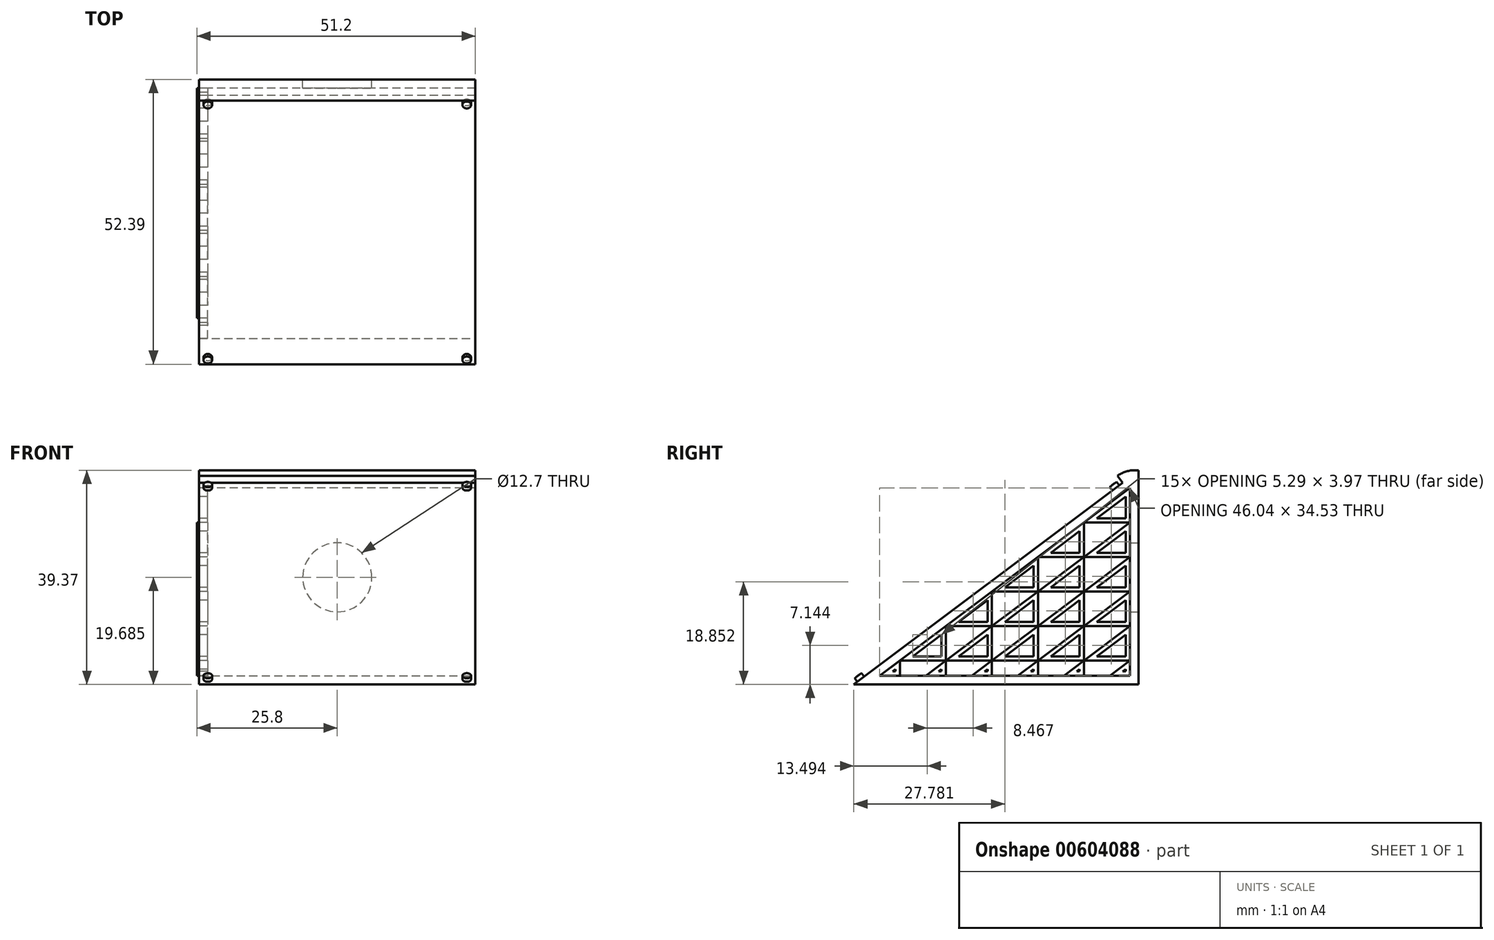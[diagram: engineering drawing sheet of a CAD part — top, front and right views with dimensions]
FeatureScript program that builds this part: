
annotation { "Feature Type Name" : "Feature", "Feature Type Description" : "" }
export const myFeature = defineFeature(function(context is Context, id is Id, definition is map)
    precondition{}
    {
        {
            var Q0;
            Q0=qCreatedBy(makeId("Right.planeOp"),FACE);
            var sketch = newSketch(context, id + "F0", { "sketchPlane" : qUnion([Q0])});
            skLineSegment(sketch, "E0.bottom", {"start": v(0, 0) * mm, "end": v(1.59, 0) * mm});
            skLineSegment(sketch, "E0.top", {"start": v(0, 38.1) * mm, "end": v(1.59, 38.1) * mm});
            skLineSegment(sketch, "E0.left", {"start": v(0, 0) * mm, "end": v(0, 36.12) * mm});
            skLineSegment(sketch, "E0.right", {"start": v(1.59, 0) * mm, "end": v(1.59, 38.1) * mm});
            skLineSegment(sketch, "E1", {"start": v(0, 38.1) * mm, "end": v(-50.8, 0) * mm});
            skLineSegment(sketch, "E2", {"start": v(-50.8, 0) * mm, "end": v(-48.15, 0) * mm});
            skLineSegment(sketch, "E3", {"start": v(-48.15, 0) * mm, "end": v(0, 36.12) * mm});
            skSolve(sketch);
        }
        {
            var Q0;
            Q0 = qSketchRegion(id + "F0", true);
            extrude(context, id + "F1", {"entities" : qUnion([Q0]), "depth" : 50.8 * mm, "offsetDistance" : 25.4 * mm});
        }
        {
            var Q0;
            Q0=makeQuery(id+"F1.opExtrude","SWEPT_FACE",FACE,{"disambiguationData":[OSD([sQuery(id+"F0.wireOp",EDGE,"E1")])]});
            var sketch = newSketch(context, id + "F2", { "sketchPlane" : qUnion([Q0])});
            skLineSegment(sketch, "E4.bottom", {"start": v(0, 22.86) * mm, "end": v(50.8, 22.86) * mm});
            skLineSegment(sketch, "E4.top", {"start": v(0, -40.64) * mm, "end": v(50.8, -40.64) * mm});
            skLineSegment(sketch, "E4.left", {"start": v(0, 22.86) * mm, "end": v(0, -40.64) * mm});
            skLineSegment(sketch, "E4.right", {"start": v(50.8, 22.86) * mm, "end": v(50.8, -40.64) * mm});
            skLineSegment(sketch, "E5.bottom", {"start": v(3.18, 19.69) * mm, "end": v(47.63, 19.69) * mm});
            skLineSegment(sketch, "E5.top", {"start": v(3.18, -37.47) * mm, "end": v(47.63, -37.47) * mm});
            skLineSegment(sketch, "E5.left", {"start": v(3.18, 19.69) * mm, "end": v(3.18, -37.47) * mm});
            skLineSegment(sketch, "E5.right", {"start": v(47.63, 19.69) * mm, "end": v(47.63, -37.47) * mm});
            skSolve(sketch);
        }
        {
            var Q0;
            Q0 = qSketchRegion(id + "F2", true);
            extrude(context, id + "F3", {"entities" : qUnion([Q0]), "operationType" : NewBodyOperationType.ADD, "depth" : 1.59 * mm, "offsetDistance" : 25.4 * mm});
        }
        {
            var Q0;
            Q0=makeQuery(id+"F3.boolean.opBoolean","MERGE",FACE,{"derivedFrom":[makeQuery(id+"F1.opExtrude","CAP_FACE",FACE,{"disambiguationData":[OSD([sQuery(id+"F0.wireOp",EDGE,"E0.bottom"),sQuery(id+"F0.wireOp",EDGE,"E0.top"),sQuery(id+"F0.wireOp",EDGE,"E0.left"),sQuery(id+"F0.wireOp",EDGE,"E0.right"),sQuery(id+"F0.wireOp",EDGE,"E1"),sQuery(id+"F0.wireOp",EDGE,"E2"),sQuery(id+"F0.wireOp",EDGE,"E3")])],"isStart":false}),makeQuery(id+"F3.opExtrude","SWEPT_FACE",FACE,{"disambiguationData":[OSD([sQuery(id+"F2.wireOp",EDGE,"E4.right")])]})]});
            var sketch = newSketch(context, id + "F4", { "sketchPlane" : qUnion([Q0])});
            skLineSegment(sketch, "E6", {"start": v(1.59, 38.1) * mm, "end": v(1.59, 39.37) * mm});
            skLineSegment(sketch, "E7", {"start": v(1.59, 39.37) * mm, "end": v(-0.95, 39.37) * mm});
            skLineSegment(sketch, "E8", {"start": v(-0.95, 39.37) * mm, "end": v(0, 38.1) * mm});
            skLineSegment(sketch, "E9", {"start": v(0, 38.1) * mm, "end": v(1.59, 38.1) * mm});
            skSolve(sketch);
        }
        {
            var Q0;
            Q0 = qSketchRegion(id + "F4", true);
            extrude(context, id + "F5", {"entities" : qUnion([Q0]), "operationType" : NewBodyOperationType.ADD, "oppositeDirection" : true, "depth" : 50.8 * mm, "offsetDistance" : 25.4 * mm});
        }
        {
            var Q0;
            Q0=makeQuery(id+"F5.boolean.opBoolean","MERGE",EDGE,{"derivedFrom":[makeQuery(id+"F3.opExtrude","CAP_EDGE",EDGE,{"disambiguationData":[OSD([sQuery(id+"F2.wireOp",EDGE,"E4.bottom")])],"isStart":false}),makeQuery(id+"F5.opExtrude","SWEPT_EDGE",EDGE,{"disambiguationData":[OSD([sQuery(id+"F2.wireOp",EDGE,"E4.right"),sQuery(id+"F4.wireOp",EDGE,"E7"),sQuery(id+"F4.wireOp",EDGE,"E8")])]})]});
            fillet(context, id + "F6", {"entities" : qUnion([Q0]), "radius" : 5.08 * mm, "tangentPropagation" : true, "allowEdgeOverflow" : false});
        }
        {
            var Q0;
            Q0=makeQuery(id+"F5.boolean.opBoolean","MERGE",FACE,{"derivedFrom":[makeQuery(id+"F1.opExtrude","SWEPT_FACE",FACE,{"disambiguationData":[OSD([sQuery(id+"F0.wireOp",EDGE,"E0.right")])]}),makeQuery(id+"F5.opExtrude","SWEPT_FACE",FACE,{"disambiguationData":[OSD([sQuery(id+"F4.wireOp",EDGE,"E6")])]})]});
            var sketch = newSketch(context, id + "F7", { "sketchPlane" : qUnion([Q0])});
            skCircle(sketch, "E10", {"center": v(-25.4, 19.69) * mm, "radius": 6.35 * mm});
            skPoint(sketch, "E10.centerSnap0", {"position": v(0, 19.69) * mm});
            skPoint(sketch, "E10.centerSnap1", {"position": v(-25.4, 39.37) * mm});
            skSolve(sketch);
        }
        {
            var Q0;
            Q0 = qSketchRegion(id + "F7", true);
            extrude(context, id + "F8", {"entities" : qUnion([Q0]), "operationType" : NewBodyOperationType.REMOVE, "oppositeDirection" : true, "depth" : 1.59 * mm, "offsetDistance" : 25.4 * mm});
        }
        {
            var Q0;
            Q0=makeQuery(id+"F3.opExtrude","CAP_FACE",FACE,{"disambiguationData":[OSD([sQuery(id+"F2.wireOp",EDGE,"E4.bottom"),sQuery(id+"F2.wireOp",EDGE,"E4.top"),sQuery(id+"F2.wireOp",EDGE,"E4.left"),sQuery(id+"F2.wireOp",EDGE,"E4.right"),sQuery(id+"F2.wireOp",EDGE,"E5.bottom"),sQuery(id+"F2.wireOp",EDGE,"E5.top"),sQuery(id+"F2.wireOp",EDGE,"E5.left"),sQuery(id+"F2.wireOp",EDGE,"E5.right")])],"isStart":false});
            var sketch = newSketch(context, id + "F9", { "sketchPlane" : qUnion([Q0])});
            skLineSegment(sketch, "E11.bottom", {"start": v(0, 21.17) * mm, "end": v(50.8, 21.17) * mm});
            skLineSegment(sketch, "E11.top", {"start": v(0, -40.64) * mm, "end": v(50.8, -40.64) * mm});
            skLineSegment(sketch, "E11.left", {"start": v(0, 21.17) * mm, "end": v(0, -40.64) * mm});
            skLineSegment(sketch, "E11.right", {"start": v(50.8, 21.17) * mm, "end": v(50.8, -40.64) * mm});
            skLineSegment(sketch, "E12.bottom", {"start": v(3.18, 19.69) * mm, "end": v(47.63, 19.69) * mm});
            skLineSegment(sketch, "E12.top", {"start": v(3.18, -37.47) * mm, "end": v(47.63, -37.47) * mm});
            skLineSegment(sketch, "E12.left", {"start": v(3.18, 19.69) * mm, "end": v(3.18, -37.47) * mm});
            skLineSegment(sketch, "E12.right", {"start": v(47.63, 19.69) * mm, "end": v(47.63, -37.47) * mm});
            skSolve(sketch);
        }
        {
            var Q0;
            Q0 = qSketchRegion(id + "F9", true);
            extrude(context, id + "F10", {"entities" : qUnion([Q0]), "operationType" : NewBodyOperationType.REMOVE, "oppositeDirection" : true, "depth" : 1.59 * mm, "offsetDistance" : 25.4 * mm});
        }
        {
            var Q0;
            Q0=makeQuery(id+"F10.boolean.opBoolean","MERGE",FACE,{"derivedFrom":[makeQuery(id+"F1.opExtrude","SWEPT_FACE",FACE,{"disambiguationData":[OSD([sQuery(id+"F0.wireOp",EDGE,"E1")])]}),makeQuery(id+"F10.opExtrude","CAP_FACE",FACE,{"disambiguationData":[OSD([sQuery(id+"F9.wireOp",EDGE,"E11.bottom"),sQuery(id+"F9.wireOp",EDGE,"E11.top"),sQuery(id+"F9.wireOp",EDGE,"E11.left"),sQuery(id+"F9.wireOp",EDGE,"E11.right"),sQuery(id+"F9.wireOp",EDGE,"E12.bottom"),sQuery(id+"F9.wireOp",EDGE,"E12.top"),sQuery(id+"F9.wireOp",EDGE,"E12.left"),sQuery(id+"F9.wireOp",EDGE,"E12.right")])],"isStart":false})]});
            var sketch = newSketch(context, id + "F11", { "sketchPlane" : qUnion([Q0])});
            skCircle(sketch, "E13", {"center": v(1.59, 19.58) * mm, "radius": 0.8 * mm});
            skCircle(sketch, "E14", {"center": v(1.59, -39.05) * mm, "radius": 0.8 * mm});
            skCircle(sketch, "E15.MirrorC", {"center": v(49.21, -39.05) * mm, "radius": 0.8 * mm});
            skCircle(sketch, "E16.MirrorC", {"center": v(49.21, 19.58) * mm, "radius": 0.8 * mm});
            skSolve(sketch);
        }
        {
            var Q0;
            Q0 = qSketchRegion(id + "F11", true);
            extrude(context, id + "F12", {"entities" : qUnion([Q0]), "operationType" : NewBodyOperationType.ADD, "depth" : 0.8 * mm, "offsetDistance" : 25.4 * mm});
        }
        {
            var Q0;
            Q0=makeQuery(id+"F5.boolean.opBoolean","MERGE",FACE,{"derivedFrom":[makeQuery(id+"F3.boolean.opBoolean","MERGE",FACE,{"derivedFrom":[makeQuery(id+"F1.opExtrude","CAP_FACE",FACE,{"disambiguationData":[OSD([sQuery(id+"F0.wireOp",EDGE,"E0.bottom"),sQuery(id+"F0.wireOp",EDGE,"E0.top"),sQuery(id+"F0.wireOp",EDGE,"E0.left"),sQuery(id+"F0.wireOp",EDGE,"E0.right"),sQuery(id+"F0.wireOp",EDGE,"E1"),sQuery(id+"F0.wireOp",EDGE,"E2"),sQuery(id+"F0.wireOp",EDGE,"E3")])],"isStart":false}),makeQuery(id+"F3.opExtrude","SWEPT_FACE",FACE,{"disambiguationData":[OSD([sQuery(id+"F2.wireOp",EDGE,"E4.right")])]})]}),makeQuery(id+"F5.opExtrude","CAP_FACE",FACE,{"disambiguationData":[OSD([sQuery(id+"F4.wireOp",EDGE,"E6"),sQuery(id+"F4.wireOp",EDGE,"E7"),sQuery(id+"F4.wireOp",EDGE,"E8"),sQuery(id+"F4.wireOp",EDGE,"E9")])],"isStart":true})]});
            var sketch = newSketch(context, id + "F13", { "sketchPlane" : qUnion([Q0])});
            skLineSegment(sketch, "E17", {"start": v(-48.15, 0) * mm, "end": v(0, 0) * mm});
            skLineSegment(sketch, "E18", {"start": v(0, 0) * mm, "end": v(0, 1.59) * mm});
            skLineSegment(sketch, "E19", {"start": v(0, 1.59) * mm, "end": v(-46.04, 1.59) * mm});
            skLineSegment(sketch, "E20", {"start": v(-48.15, 0) * mm, "end": v(-46.04, 1.59) * mm});
            skLineSegment(sketch, "E21", {"start": v(0, 1.59) * mm, "end": v(0, 0) * mm});
            skSolve(sketch);
        }
        {
            var Q0;
            Q0 = qSketchRegion(id + "F13", true);
            extrude(context, id + "F14", {"entities" : qUnion([Q0]), "operationType" : NewBodyOperationType.ADD, "oppositeDirection" : true, "depth" : 50.8 * mm, "offsetDistance" : 25.4 * mm});
        }
        {
            var Q0;
            Q0=makeQuery(id+"F14.boolean.opBoolean","MERGE",FACE,{"derivedFrom":[makeQuery(id+"F5.boolean.opBoolean","MERGE",FACE,{"derivedFrom":[makeQuery(id+"F3.boolean.opBoolean","MERGE",FACE,{"derivedFrom":[makeQuery(id+"F1.opExtrude","CAP_FACE",FACE,{"disambiguationData":[OSD([sQuery(id+"F0.wireOp",EDGE,"E0.bottom"),sQuery(id+"F0.wireOp",EDGE,"E0.top"),sQuery(id+"F0.wireOp",EDGE,"E0.left"),sQuery(id+"F0.wireOp",EDGE,"E0.right"),sQuery(id+"F0.wireOp",EDGE,"E1"),sQuery(id+"F0.wireOp",EDGE,"E2"),sQuery(id+"F0.wireOp",EDGE,"E3")])],"isStart":true}),makeQuery(id+"F3.opExtrude","SWEPT_FACE",FACE,{"disambiguationData":[OSD([sQuery(id+"F2.wireOp",EDGE,"E4.left")])]})]}),makeQuery(id+"F5.opExtrude","CAP_FACE",FACE,{"disambiguationData":[OSD([sQuery(id+"F4.wireOp",EDGE,"E6"),sQuery(id+"F4.wireOp",EDGE,"E7"),sQuery(id+"F4.wireOp",EDGE,"E8"),sQuery(id+"F4.wireOp",EDGE,"E9")])],"isStart":false})]}),makeQuery(id+"F14.opExtrude","CAP_FACE",FACE,{"disambiguationData":[OSD([sQuery(id+"F13.wireOp",EDGE,"E17"),sQuery(id+"F13.wireOp",EDGE,"E19"),sQuery(id+"F13.wireOp",EDGE,"E20"),sQuery(id+"F13.wireOp",EDGE,"E21")])],"isStart":false})]});
            var sketch = newSketch(context, id + "F15", { "sketchPlane" : qUnion([Q0])});
            skLineSegment(sketch, "E22", {"start": v(0, 29.77) * mm, "end": v(37.57, 1.59) * mm});
            skLineSegment(sketch, "E23", {"start": v(0, 23.42) * mm, "end": v(29.1, 1.59) * mm});
            skLineSegment(sketch, "E24", {"start": v(0, 17.07) * mm, "end": v(20.64, 1.59) * mm});
            skLineSegment(sketch, "E25", {"start": v(0, 10.72) * mm, "end": v(12.17, 1.59) * mm});
            skLineSegment(sketch, "E26", {"start": v(0, 4.37) * mm, "end": v(3.7, 1.59) * mm});
            skLineSegment(sketch, "E27", {"start": v(0, 4.37) * mm, "end": v(42.33, 4.37) * mm});
            skLineSegment(sketch, "E28", {"start": v(0, 10.72) * mm, "end": v(33.87, 10.72) * mm});
            skLineSegment(sketch, "E29", {"start": v(0, 17.07) * mm, "end": v(25.4, 17.07) * mm});
            skLineSegment(sketch, "E30", {"start": v(0, 23.42) * mm, "end": v(16.93, 23.42) * mm});
            skLineSegment(sketch, "E31", {"start": v(0, 29.77) * mm, "end": v(8.47, 29.77) * mm});
            skLineSegment(sketch, "E32", {"start": v(8.47, 29.77) * mm, "end": v(8.47, 1.59) * mm});
            skLineSegment(sketch, "E33", {"start": v(16.93, 23.42) * mm, "end": v(16.93, 1.59) * mm});
            skLineSegment(sketch, "E34", {"start": v(25.4, 17.07) * mm, "end": v(25.4, 1.59) * mm});
            skLineSegment(sketch, "E35", {"start": v(33.87, 10.72) * mm, "end": v(33.87, 1.59) * mm});
            skLineSegment(sketch, "E36", {"start": v(42.33, 4.37) * mm, "end": v(42.33, 1.59) * mm});
            skSolve(sketch);
        }
        {
            var Q0;
            {var subQ0=sQuery(id+"F15.wireOp",EDGE,"E31");Q0=makeQuery(id+"F15.imprint","IMPRINT",FACE,{"disambiguationData":[TD([[makeQuery(id+"F15.imprint","IMPRINT",EDGE,{"derivedFrom":subQ0}),1.0]])]});}
            var Q1;
            {var subQ0=sQuery(id+"F15.wireOp",EDGE,"E30");var subQ1=makeQuery(id+"F1.opExtrude","CAP_EDGE",EDGE,{"disambiguationData":[OSD([sQuery(id+"F0.wireOp",EDGE,"E3")])],"isStart":true});var subQ2=makeQuery(id+"F15.imprint","INTERSECT",VERTEX,{"derivedFrom":[subQ1,subQ0,sQuery(id+"F15.wireOp",EDGE,"E33")]});Q1=makeQuery(id+"F15.imprint","IMPRINT",FACE,{"disambiguationData":[TD([[makeQuery(id+"F15.imprint","IMPRINT",EDGE,{"disambiguationData":[TD([[subQ2,1.0]])],"derivedFrom":subQ0}),1.0]])]});}
            var Q2;
            {var subQ0=sQuery(id+"F15.wireOp",EDGE,"E29");var subQ1=makeQuery(id+"F1.opExtrude","CAP_EDGE",EDGE,{"disambiguationData":[OSD([sQuery(id+"F0.wireOp",EDGE,"E3")])],"isStart":true});var subQ2=makeQuery(id+"F15.imprint","INTERSECT",VERTEX,{"derivedFrom":[subQ1,subQ0,sQuery(id+"F15.wireOp",EDGE,"E34")]});Q2=makeQuery(id+"F15.imprint","IMPRINT",FACE,{"disambiguationData":[TD([[makeQuery(id+"F15.imprint","IMPRINT",EDGE,{"disambiguationData":[TD([[subQ2,1.0]])],"derivedFrom":subQ0}),1.0]])]});}
            var Q3;
            {var subQ0=sQuery(id+"F15.wireOp",EDGE,"E28");var subQ1=makeQuery(id+"F1.opExtrude","CAP_EDGE",EDGE,{"disambiguationData":[OSD([sQuery(id+"F0.wireOp",EDGE,"E3")])],"isStart":true});var subQ2=makeQuery(id+"F15.imprint","INTERSECT",VERTEX,{"derivedFrom":[subQ1,subQ0,sQuery(id+"F15.wireOp",EDGE,"E35")]});Q3=makeQuery(id+"F15.imprint","IMPRINT",FACE,{"disambiguationData":[TD([[makeQuery(id+"F15.imprint","IMPRINT",EDGE,{"disambiguationData":[TD([[subQ2,1.0]])],"derivedFrom":subQ0}),1.0]])]});}
            var Q4;
            {var subQ0=sQuery(id+"F15.wireOp",EDGE,"E27");var subQ1=makeQuery(id+"F1.opExtrude","CAP_EDGE",EDGE,{"disambiguationData":[OSD([sQuery(id+"F0.wireOp",EDGE,"E3")])],"isStart":true});var subQ2=makeQuery(id+"F15.imprint","INTERSECT",VERTEX,{"derivedFrom":[subQ1,subQ0,sQuery(id+"F15.wireOp",EDGE,"E36")]});Q4=makeQuery(id+"F15.imprint","IMPRINT",FACE,{"disambiguationData":[TD([[makeQuery(id+"F15.imprint","IMPRINT",EDGE,{"disambiguationData":[TD([[subQ2,1.0]])],"derivedFrom":subQ0}),1.0]])]});}
            var Q5;
            {var subQ0=sQuery(id+"F15.wireOp",EDGE,"E36");Q5=makeQuery(id+"F15.imprint","IMPRINT",FACE,{"disambiguationData":[TD([[makeQuery(id+"F15.imprint","IMPRINT",EDGE,{"derivedFrom":subQ0}),1.0]])]});}
            var Q6;
            {var subQ0=sQuery(id+"F15.wireOp",EDGE,"E22");var subQ1=makeQuery(id+"F14.opExtrude","CAP_EDGE",EDGE,{"disambiguationData":[OSD([sQuery(id+"F13.wireOp",EDGE,"E19")])],"isStart":false});var subQ2=makeQuery(id+"F15.imprint","INTERSECT",VERTEX,{"derivedFrom":[subQ1,subQ0]});Q6=makeQuery(id+"F15.imprint","IMPRINT",FACE,{"disambiguationData":[TD([[makeQuery(id+"F15.imprint","IMPRINT",EDGE,{"disambiguationData":[TD([[subQ2,1.0]])],"derivedFrom":subQ1}),1.0]])]});}
            var Q7;
            {var subQ0=sQuery(id+"F15.wireOp",EDGE,"E34");var subQ1=sQuery(id+"F15.wireOp",EDGE,"E22");var subQ2=makeQuery(id+"F15.imprint","INTERSECT",VERTEX,{"derivedFrom":[subQ1,sQuery(id+"F15.wireOp",EDGE,"E28"),subQ0]});Q7=makeQuery(id+"F15.imprint","IMPRINT",FACE,{"disambiguationData":[TD([[makeQuery(id+"F15.imprint","IMPRINT",EDGE,{"disambiguationData":[TD([[subQ2,-1.0]])],"derivedFrom":subQ1}),-1.0]])]});}
            var Q8;
            {var subQ0=sQuery(id+"F15.wireOp",EDGE,"E23");var subQ1=makeQuery(id+"F14.opExtrude","CAP_EDGE",EDGE,{"disambiguationData":[OSD([sQuery(id+"F13.wireOp",EDGE,"E19")])],"isStart":false});var subQ2=makeQuery(id+"F15.imprint","INTERSECT",VERTEX,{"derivedFrom":[subQ1,subQ0]});Q8=makeQuery(id+"F15.imprint","IMPRINT",FACE,{"disambiguationData":[TD([[makeQuery(id+"F15.imprint","IMPRINT",EDGE,{"disambiguationData":[TD([[subQ2,1.0]])],"derivedFrom":subQ1}),1.0]])]});}
            var Q9;
            {var subQ0=sQuery(id+"F15.wireOp",EDGE,"E24");var subQ1=makeQuery(id+"F14.opExtrude","CAP_EDGE",EDGE,{"disambiguationData":[OSD([sQuery(id+"F13.wireOp",EDGE,"E19")])],"isStart":false});var subQ2=makeQuery(id+"F15.imprint","INTERSECT",VERTEX,{"derivedFrom":[subQ1,subQ0]});Q9=makeQuery(id+"F15.imprint","IMPRINT",FACE,{"disambiguationData":[TD([[makeQuery(id+"F15.imprint","IMPRINT",EDGE,{"disambiguationData":[TD([[subQ2,1.0]])],"derivedFrom":subQ1}),1.0]])]});}
            var Q10;
            {var subQ0=sQuery(id+"F15.wireOp",EDGE,"E25");var subQ1=makeQuery(id+"F14.opExtrude","CAP_EDGE",EDGE,{"disambiguationData":[OSD([sQuery(id+"F13.wireOp",EDGE,"E19")])],"isStart":false});var subQ2=makeQuery(id+"F15.imprint","INTERSECT",VERTEX,{"derivedFrom":[subQ1,subQ0]});Q10=makeQuery(id+"F15.imprint","IMPRINT",FACE,{"disambiguationData":[TD([[makeQuery(id+"F15.imprint","IMPRINT",EDGE,{"disambiguationData":[TD([[subQ2,1.0]])],"derivedFrom":subQ1}),1.0]])]});}
            var Q11;
            {var subQ0=sQuery(id+"F15.wireOp",EDGE,"E26");Q11=makeQuery(id+"F15.imprint","IMPRINT",FACE,{"disambiguationData":[TD([[makeQuery(id+"F15.imprint","IMPRINT",EDGE,{"derivedFrom":subQ0}),-1.0]])]});}
            var Q12;
            {var subQ0=sQuery(id+"F15.wireOp",EDGE,"E25");var subQ1=makeQuery(id+"F1.opExtrude","CAP_EDGE",EDGE,{"disambiguationData":[OSD([sQuery(id+"F0.wireOp",EDGE,"E0.left")])],"isStart":true});var subQ2=makeQuery(id+"F15.imprint","INTERSECT",VERTEX,{"derivedFrom":[subQ1,subQ0,sQuery(id+"F15.wireOp",EDGE,"E28")]});Q12=makeQuery(id+"F15.imprint","IMPRINT",FACE,{"disambiguationData":[TD([[makeQuery(id+"F15.imprint","IMPRINT",EDGE,{"disambiguationData":[TD([[subQ2,-1.0]])],"derivedFrom":subQ0}),-1.0]])]});}
            var Q13;
            {var subQ0=sQuery(id+"F15.wireOp",EDGE,"E24");var subQ1=makeQuery(id+"F1.opExtrude","CAP_EDGE",EDGE,{"disambiguationData":[OSD([sQuery(id+"F0.wireOp",EDGE,"E0.left")])],"isStart":true});var subQ2=makeQuery(id+"F15.imprint","INTERSECT",VERTEX,{"derivedFrom":[subQ1,subQ0,sQuery(id+"F15.wireOp",EDGE,"E29")]});Q13=makeQuery(id+"F15.imprint","IMPRINT",FACE,{"disambiguationData":[TD([[makeQuery(id+"F15.imprint","IMPRINT",EDGE,{"disambiguationData":[TD([[subQ2,-1.0]])],"derivedFrom":subQ0}),-1.0]])]});}
            var Q14;
            {var subQ0=sQuery(id+"F15.wireOp",EDGE,"E23");var subQ1=makeQuery(id+"F1.opExtrude","CAP_EDGE",EDGE,{"disambiguationData":[OSD([sQuery(id+"F0.wireOp",EDGE,"E0.left")])],"isStart":true});var subQ2=makeQuery(id+"F15.imprint","INTERSECT",VERTEX,{"derivedFrom":[subQ1,subQ0,sQuery(id+"F15.wireOp",EDGE,"E30")]});Q14=makeQuery(id+"F15.imprint","IMPRINT",FACE,{"disambiguationData":[TD([[makeQuery(id+"F15.imprint","IMPRINT",EDGE,{"disambiguationData":[TD([[subQ2,-1.0]])],"derivedFrom":subQ0}),-1.0]])]});}
            var Q15;
            {var subQ0=sQuery(id+"F15.wireOp",EDGE,"E22");var subQ1=makeQuery(id+"F1.opExtrude","CAP_EDGE",EDGE,{"disambiguationData":[OSD([sQuery(id+"F0.wireOp",EDGE,"E0.left")])],"isStart":true});var subQ2=makeQuery(id+"F15.imprint","INTERSECT",VERTEX,{"derivedFrom":[subQ1,subQ0,sQuery(id+"F15.wireOp",EDGE,"E31")]});Q15=makeQuery(id+"F15.imprint","IMPRINT",FACE,{"disambiguationData":[TD([[makeQuery(id+"F15.imprint","IMPRINT",EDGE,{"disambiguationData":[TD([[subQ2,-1.0]])],"derivedFrom":subQ0}),-1.0]])]});}
            var Q16;
            {var subQ0=sQuery(id+"F15.wireOp",EDGE,"E32");var subQ1=sQuery(id+"F15.wireOp",EDGE,"E22");var subQ2=makeQuery(id+"F15.imprint","INTERSECT",VERTEX,{"derivedFrom":[subQ1,sQuery(id+"F15.wireOp",EDGE,"E30"),subQ0]});Q16=makeQuery(id+"F15.imprint","IMPRINT",FACE,{"disambiguationData":[TD([[makeQuery(id+"F15.imprint","IMPRINT",EDGE,{"disambiguationData":[TD([[subQ2,-1.0]])],"derivedFrom":subQ1}),-1.0]])]});}
            var Q17;
            {var subQ0=sQuery(id+"F15.wireOp",EDGE,"E32");var subQ1=sQuery(id+"F15.wireOp",EDGE,"E23");var subQ2=makeQuery(id+"F15.imprint","INTERSECT",VERTEX,{"derivedFrom":[subQ1,sQuery(id+"F15.wireOp",EDGE,"E29"),subQ0]});Q17=makeQuery(id+"F15.imprint","IMPRINT",FACE,{"disambiguationData":[TD([[makeQuery(id+"F15.imprint","IMPRINT",EDGE,{"disambiguationData":[TD([[subQ2,-1.0]])],"derivedFrom":subQ1}),-1.0]])]});}
            var Q18;
            {var subQ0=sQuery(id+"F15.wireOp",EDGE,"E32");var subQ1=sQuery(id+"F15.wireOp",EDGE,"E24");var subQ2=makeQuery(id+"F15.imprint","INTERSECT",VERTEX,{"derivedFrom":[subQ1,sQuery(id+"F15.wireOp",EDGE,"E28"),subQ0]});Q18=makeQuery(id+"F15.imprint","IMPRINT",FACE,{"disambiguationData":[TD([[makeQuery(id+"F15.imprint","IMPRINT",EDGE,{"disambiguationData":[TD([[subQ2,-1.0]])],"derivedFrom":subQ1}),-1.0]])]});}
            var Q19;
            {var subQ0=sQuery(id+"F15.wireOp",EDGE,"E33");var subQ1=sQuery(id+"F15.wireOp",EDGE,"E22");var subQ2=makeQuery(id+"F15.imprint","INTERSECT",VERTEX,{"derivedFrom":[subQ1,sQuery(id+"F15.wireOp",EDGE,"E29"),subQ0]});Q19=makeQuery(id+"F15.imprint","IMPRINT",FACE,{"disambiguationData":[TD([[makeQuery(id+"F15.imprint","IMPRINT",EDGE,{"disambiguationData":[TD([[subQ2,-1.0]])],"derivedFrom":subQ1}),-1.0]])]});}
            var Q20;
            {var subQ0=sQuery(id+"F15.wireOp",EDGE,"E33");var subQ1=sQuery(id+"F15.wireOp",EDGE,"E23");var subQ2=makeQuery(id+"F15.imprint","INTERSECT",VERTEX,{"derivedFrom":[subQ1,sQuery(id+"F15.wireOp",EDGE,"E28"),subQ0]});Q20=makeQuery(id+"F15.imprint","IMPRINT",FACE,{"disambiguationData":[TD([[makeQuery(id+"F15.imprint","IMPRINT",EDGE,{"disambiguationData":[TD([[subQ2,-1.0]])],"derivedFrom":subQ1}),-1.0]])]});}
            extrude(context, id + "F16", {"entities" : qUnion([Q0, Q1, Q2, Q3, Q4, Q5, Q6, Q7, Q8, Q9, Q10, Q11, Q12, Q13, Q14, Q15, Q16, Q17, Q18, Q19, Q20]), "oppositeDirection" : true, "depth" : 1.59 * mm, "offsetDistance" : 25.4 * mm});
        }
        {
            var Q0;
            Q0=makeQuery(id+"F16.opExtrude","CAP_FACE",FACE,{"disambiguationData":[OSD([sQuery(id+"F0.wireOp",EDGE,"E0.left"),sQuery(id+"F0.wireOp",EDGE,"E3"),sQuery(id+"F15.wireOp",EDGE,"E31")])],"isStart":true});
            var Q1;
            Q1=makeQuery(id+"F16.opExtrude","CAP_FACE",FACE,{"disambiguationData":[OSD([sQuery(id+"F0.wireOp",EDGE,"E0.left"),sQuery(id+"F0.wireOp",EDGE,"E3"),sQuery(id+"F15.wireOp",EDGE,"E31")])],"isStart":false});
            var Q2;
            Q2=makeQuery(id+"F16.opExtrude","CAP_FACE",FACE,{"disambiguationData":[OSD([sQuery(id+"F0.wireOp",EDGE,"E0.left"),sQuery(id+"F15.wireOp",EDGE,"E22"),sQuery(id+"F15.wireOp",EDGE,"E30")])],"isStart":true});
            var Q3;
            Q3=makeQuery(id+"F16.opExtrude","CAP_FACE",FACE,{"disambiguationData":[OSD([sQuery(id+"F0.wireOp",EDGE,"E0.left"),sQuery(id+"F15.wireOp",EDGE,"E22"),sQuery(id+"F15.wireOp",EDGE,"E30")])],"isStart":false});
            var Q4;
            Q4=makeQuery(id+"F16.opExtrude","CAP_FACE",FACE,{"disambiguationData":[OSD([sQuery(id+"F0.wireOp",EDGE,"E0.left"),sQuery(id+"F15.wireOp",EDGE,"E23"),sQuery(id+"F15.wireOp",EDGE,"E29")])],"isStart":false});
            var Q5;
            Q5=makeQuery(id+"F16.opExtrude","CAP_FACE",FACE,{"disambiguationData":[OSD([sQuery(id+"F15.wireOp",EDGE,"E22"),sQuery(id+"F15.wireOp",EDGE,"E29"),sQuery(id+"F15.wireOp",EDGE,"E32")])],"isStart":false});
            var Q6;
            Q6=makeQuery(id+"F16.opExtrude","CAP_FACE",FACE,{"disambiguationData":[OSD([sQuery(id+"F0.wireOp",EDGE,"E3"),sQuery(id+"F15.wireOp",EDGE,"E30"),sQuery(id+"F15.wireOp",EDGE,"E32")])],"isStart":false});
            var Q7;
            Q7=makeQuery(id+"F16.opExtrude","CAP_FACE",FACE,{"disambiguationData":[OSD([sQuery(id+"F0.wireOp",EDGE,"E0.left"),sQuery(id+"F15.wireOp",EDGE,"E24"),sQuery(id+"F15.wireOp",EDGE,"E28")])],"isStart":false});
            var Q8;
            Q8=makeQuery(id+"F16.opExtrude","CAP_FACE",FACE,{"disambiguationData":[OSD([sQuery(id+"F15.wireOp",EDGE,"E23"),sQuery(id+"F15.wireOp",EDGE,"E28"),sQuery(id+"F15.wireOp",EDGE,"E32")])],"isStart":false});
            var Q9;
            Q9=makeQuery(id+"F16.opExtrude","CAP_FACE",FACE,{"disambiguationData":[OSD([sQuery(id+"F15.wireOp",EDGE,"E22"),sQuery(id+"F15.wireOp",EDGE,"E28"),sQuery(id+"F15.wireOp",EDGE,"E33")])],"isStart":false});
            var Q10;
            Q10=makeQuery(id+"F16.opExtrude","CAP_FACE",FACE,{"disambiguationData":[OSD([sQuery(id+"F15.wireOp",EDGE,"E24"),sQuery(id+"F15.wireOp",EDGE,"E27"),sQuery(id+"F15.wireOp",EDGE,"E32")])],"isStart":false});
            var Q11;
            Q11=makeQuery(id+"F16.opExtrude","CAP_FACE",FACE,{"disambiguationData":[OSD([sQuery(id+"F0.wireOp",EDGE,"E0.left"),sQuery(id+"F15.wireOp",EDGE,"E25"),sQuery(id+"F15.wireOp",EDGE,"E27")])],"isStart":false});
            var Q12;
            Q12=makeQuery(id+"F16.opExtrude","CAP_FACE",FACE,{"disambiguationData":[OSD([sQuery(id+"F15.wireOp",EDGE,"E23"),sQuery(id+"F15.wireOp",EDGE,"E27"),sQuery(id+"F15.wireOp",EDGE,"E33")])],"isStart":false});
            var Q13;
            Q13=makeQuery(id+"F16.opExtrude","CAP_FACE",FACE,{"disambiguationData":[OSD([sQuery(id+"F0.wireOp",EDGE,"E3"),sQuery(id+"F15.wireOp",EDGE,"E29"),sQuery(id+"F15.wireOp",EDGE,"E33")])],"isStart":false});
            var Q14;
            Q14=makeQuery(id+"F16.opExtrude","CAP_FACE",FACE,{"disambiguationData":[OSD([sQuery(id+"F0.wireOp",EDGE,"E3"),sQuery(id+"F15.wireOp",EDGE,"E28"),sQuery(id+"F15.wireOp",EDGE,"E34")])],"isStart":false});
            var Q15;
            Q15=makeQuery(id+"F16.opExtrude","CAP_FACE",FACE,{"disambiguationData":[OSD([sQuery(id+"F15.wireOp",EDGE,"E22"),sQuery(id+"F15.wireOp",EDGE,"E27"),sQuery(id+"F15.wireOp",EDGE,"E34")])],"isStart":false});
            var Q16;
            Q16=makeQuery(id+"F16.opExtrude","CAP_FACE",FACE,{"disambiguationData":[OSD([sQuery(id+"F0.wireOp",EDGE,"E3"),sQuery(id+"F15.wireOp",EDGE,"E27"),sQuery(id+"F15.wireOp",EDGE,"E35")])],"isStart":false});
            var Q17;
            Q17=makeQuery(id+"F16.opExtrude","CAP_FACE",FACE,{"disambiguationData":[OSD([sQuery(id+"F0.wireOp",EDGE,"E3"),sQuery(id+"F15.wireOp",EDGE,"E30"),sQuery(id+"F15.wireOp",EDGE,"E32")])],"isStart":true});
            var Q18;
            Q18=makeQuery(id+"F16.opExtrude","CAP_FACE",FACE,{"disambiguationData":[OSD([sQuery(id+"F0.wireOp",EDGE,"E3"),sQuery(id+"F15.wireOp",EDGE,"E29"),sQuery(id+"F15.wireOp",EDGE,"E33")])],"isStart":true});
            var Q19;
            Q19=makeQuery(id+"F16.opExtrude","CAP_FACE",FACE,{"disambiguationData":[OSD([sQuery(id+"F15.wireOp",EDGE,"E22"),sQuery(id+"F15.wireOp",EDGE,"E29"),sQuery(id+"F15.wireOp",EDGE,"E32")])],"isStart":true});
            var Q20;
            Q20=makeQuery(id+"F16.opExtrude","CAP_FACE",FACE,{"disambiguationData":[OSD([sQuery(id+"F0.wireOp",EDGE,"E0.left"),sQuery(id+"F15.wireOp",EDGE,"E23"),sQuery(id+"F15.wireOp",EDGE,"E29")])],"isStart":true});
            var Q21;
            Q21=makeQuery(id+"F16.opExtrude","CAP_FACE",FACE,{"disambiguationData":[OSD([sQuery(id+"F0.wireOp",EDGE,"E0.left"),sQuery(id+"F15.wireOp",EDGE,"E24"),sQuery(id+"F15.wireOp",EDGE,"E28")])],"isStart":true});
            var Q22;
            Q22=makeQuery(id+"F16.opExtrude","CAP_FACE",FACE,{"disambiguationData":[OSD([sQuery(id+"F15.wireOp",EDGE,"E23"),sQuery(id+"F15.wireOp",EDGE,"E28"),sQuery(id+"F15.wireOp",EDGE,"E32")])],"isStart":true});
            var Q23;
            Q23=makeQuery(id+"F16.opExtrude","CAP_FACE",FACE,{"disambiguationData":[OSD([sQuery(id+"F15.wireOp",EDGE,"E24"),sQuery(id+"F15.wireOp",EDGE,"E27"),sQuery(id+"F15.wireOp",EDGE,"E32")])],"isStart":true});
            var Q24;
            Q24=makeQuery(id+"F16.opExtrude","CAP_FACE",FACE,{"disambiguationData":[OSD([sQuery(id+"F0.wireOp",EDGE,"E0.left"),sQuery(id+"F15.wireOp",EDGE,"E25"),sQuery(id+"F15.wireOp",EDGE,"E27")])],"isStart":true});
            var Q25;
            Q25=makeQuery(id+"F16.opExtrude","CAP_FACE",FACE,{"disambiguationData":[OSD([sQuery(id+"F15.wireOp",EDGE,"E22"),sQuery(id+"F15.wireOp",EDGE,"E28"),sQuery(id+"F15.wireOp",EDGE,"E33")])],"isStart":true});
            var Q26;
            Q26=makeQuery(id+"F16.opExtrude","CAP_FACE",FACE,{"disambiguationData":[OSD([sQuery(id+"F15.wireOp",EDGE,"E23"),sQuery(id+"F15.wireOp",EDGE,"E27"),sQuery(id+"F15.wireOp",EDGE,"E33")])],"isStart":true});
            var Q27;
            Q27=makeQuery(id+"F16.opExtrude","CAP_FACE",FACE,{"disambiguationData":[OSD([sQuery(id+"F0.wireOp",EDGE,"E3"),sQuery(id+"F15.wireOp",EDGE,"E28"),sQuery(id+"F15.wireOp",EDGE,"E34")])],"isStart":true});
            var Q28;
            Q28=makeQuery(id+"F16.opExtrude","CAP_FACE",FACE,{"disambiguationData":[OSD([sQuery(id+"F15.wireOp",EDGE,"E22"),sQuery(id+"F15.wireOp",EDGE,"E27"),sQuery(id+"F15.wireOp",EDGE,"E34")])],"isStart":true});
            var Q29;
            Q29=makeQuery(id+"F16.opExtrude","CAP_FACE",FACE,{"disambiguationData":[OSD([sQuery(id+"F0.wireOp",EDGE,"E3"),sQuery(id+"F15.wireOp",EDGE,"E27"),sQuery(id+"F15.wireOp",EDGE,"E35")])],"isStart":true});
            var Q30;
            Q30=makeQuery(id+"F16.opExtrude","CAP_FACE",FACE,{"disambiguationData":[OSD([sQuery(id+"F0.wireOp",EDGE,"E3"),sQuery(id+"F13.wireOp",EDGE,"E19"),sQuery(id+"F15.wireOp",EDGE,"E36")])],"isStart":true});
            var Q31;
            Q31=makeQuery(id+"F16.opExtrude","CAP_FACE",FACE,{"disambiguationData":[OSD([sQuery(id+"F13.wireOp",EDGE,"E19"),sQuery(id+"F15.wireOp",EDGE,"E22"),sQuery(id+"F15.wireOp",EDGE,"E35")])],"isStart":true});
            var Q32;
            Q32=makeQuery(id+"F16.opExtrude","CAP_FACE",FACE,{"disambiguationData":[OSD([sQuery(id+"F13.wireOp",EDGE,"E19"),sQuery(id+"F15.wireOp",EDGE,"E23"),sQuery(id+"F15.wireOp",EDGE,"E34")])],"isStart":true});
            var Q33;
            Q33=makeQuery(id+"F16.opExtrude","CAP_FACE",FACE,{"disambiguationData":[OSD([sQuery(id+"F13.wireOp",EDGE,"E19"),sQuery(id+"F15.wireOp",EDGE,"E24"),sQuery(id+"F15.wireOp",EDGE,"E33")])],"isStart":true});
            var Q34;
            Q34=makeQuery(id+"F16.opExtrude","CAP_FACE",FACE,{"disambiguationData":[OSD([sQuery(id+"F13.wireOp",EDGE,"E19"),sQuery(id+"F15.wireOp",EDGE,"E25"),sQuery(id+"F15.wireOp",EDGE,"E32")])],"isStart":true});
            var Q35;
            Q35=makeQuery(id+"F16.opExtrude","CAP_FACE",FACE,{"disambiguationData":[OSD([sQuery(id+"F0.wireOp",EDGE,"E0.left"),sQuery(id+"F13.wireOp",EDGE,"E19"),sQuery(id+"F15.wireOp",EDGE,"E26")])],"isStart":true});
            var Q36;
            Q36=makeQuery(id+"F16.opExtrude","CAP_FACE",FACE,{"disambiguationData":[OSD([sQuery(id+"F0.wireOp",EDGE,"E0.left"),sQuery(id+"F13.wireOp",EDGE,"E19"),sQuery(id+"F15.wireOp",EDGE,"E26")])],"isStart":false});
            var Q37;
            Q37=makeQuery(id+"F16.opExtrude","CAP_FACE",FACE,{"disambiguationData":[OSD([sQuery(id+"F13.wireOp",EDGE,"E19"),sQuery(id+"F15.wireOp",EDGE,"E25"),sQuery(id+"F15.wireOp",EDGE,"E32")])],"isStart":false});
            var Q38;
            Q38=makeQuery(id+"F16.opExtrude","CAP_FACE",FACE,{"disambiguationData":[OSD([sQuery(id+"F13.wireOp",EDGE,"E19"),sQuery(id+"F15.wireOp",EDGE,"E24"),sQuery(id+"F15.wireOp",EDGE,"E33")])],"isStart":false});
            var Q39;
            Q39=makeQuery(id+"F16.opExtrude","CAP_FACE",FACE,{"disambiguationData":[OSD([sQuery(id+"F13.wireOp",EDGE,"E19"),sQuery(id+"F15.wireOp",EDGE,"E23"),sQuery(id+"F15.wireOp",EDGE,"E34")])],"isStart":false});
            var Q40;
            Q40=makeQuery(id+"F16.opExtrude","CAP_FACE",FACE,{"disambiguationData":[OSD([sQuery(id+"F13.wireOp",EDGE,"E19"),sQuery(id+"F15.wireOp",EDGE,"E22"),sQuery(id+"F15.wireOp",EDGE,"E35")])],"isStart":false});
            var Q41;
            Q41=makeQuery(id+"F16.opExtrude","CAP_FACE",FACE,{"disambiguationData":[OSD([sQuery(id+"F0.wireOp",EDGE,"E3"),sQuery(id+"F13.wireOp",EDGE,"E19"),sQuery(id+"F15.wireOp",EDGE,"E36")])],"isStart":false});
            shell(context, id + "F17", {"entities" : qUnion([Q0, Q1, Q2, Q3, Q4, Q5, Q6, Q7, Q8, Q9, Q10, Q11, Q12, Q13, Q14, Q15, Q16, Q17, Q18, Q19, Q20, Q21, Q22, Q23, Q24, Q25, Q26, Q27, Q28, Q29, Q30, Q31, Q32, Q33, Q34, Q35, Q36, Q37, Q38, Q39, Q40, Q41]), "thickness" : 0.8 * mm});
        }
        {
            var Q0;
            {var subQ0=sQuery(id+"F15.wireOp",EDGE,"E31");Q0=makeQuery(id+"F15.imprint","IMPRINT",FACE,{"disambiguationData":[TD([[makeQuery(id+"F15.imprint","IMPRINT",EDGE,{"derivedFrom":subQ0}),-1.0]])]});}
            var Q1;
            {var subQ0=sQuery(id+"F15.wireOp",EDGE,"E30");var subQ1=sQuery(id+"F15.wireOp",EDGE,"E23");var subQ2=makeQuery(id+"F15.imprint","INTERSECT",VERTEX,{"derivedFrom":[makeQuery(id+"F1.opExtrude","CAP_EDGE",EDGE,{"disambiguationData":[OSD([sQuery(id+"F0.wireOp",EDGE,"E0.left")])],"isStart":true}),subQ1,subQ0]});Q1=makeQuery(id+"F15.imprint","IMPRINT",FACE,{"disambiguationData":[TD([[makeQuery(id+"F15.imprint","IMPRINT",EDGE,{"disambiguationData":[TD([[subQ2,-1.0]])],"derivedFrom":subQ1}),1.0]])]});}
            var Q2;
            {var subQ0=sQuery(id+"F15.wireOp",EDGE,"E29");var subQ1=sQuery(id+"F15.wireOp",EDGE,"E24");var subQ2=makeQuery(id+"F15.imprint","INTERSECT",VERTEX,{"derivedFrom":[makeQuery(id+"F1.opExtrude","CAP_EDGE",EDGE,{"disambiguationData":[OSD([sQuery(id+"F0.wireOp",EDGE,"E0.left")])],"isStart":true}),subQ1,subQ0]});Q2=makeQuery(id+"F15.imprint","IMPRINT",FACE,{"disambiguationData":[TD([[makeQuery(id+"F15.imprint","IMPRINT",EDGE,{"disambiguationData":[TD([[subQ2,-1.0]])],"derivedFrom":subQ1}),1.0]])]});}
            var Q3;
            {var subQ0=sQuery(id+"F15.wireOp",EDGE,"E28");var subQ1=sQuery(id+"F15.wireOp",EDGE,"E25");var subQ2=makeQuery(id+"F15.imprint","INTERSECT",VERTEX,{"derivedFrom":[makeQuery(id+"F1.opExtrude","CAP_EDGE",EDGE,{"disambiguationData":[OSD([sQuery(id+"F0.wireOp",EDGE,"E0.left")])],"isStart":true}),subQ1,subQ0]});Q3=makeQuery(id+"F15.imprint","IMPRINT",FACE,{"disambiguationData":[TD([[makeQuery(id+"F15.imprint","IMPRINT",EDGE,{"disambiguationData":[TD([[subQ2,-1.0]])],"derivedFrom":subQ1}),1.0]])]});}
            var Q4;
            {var subQ0=sQuery(id+"F15.wireOp",EDGE,"E26");Q4=makeQuery(id+"F15.imprint","IMPRINT",FACE,{"disambiguationData":[TD([[makeQuery(id+"F15.imprint","IMPRINT",EDGE,{"derivedFrom":subQ0}),1.0]])]});}
            var Q5;
            {var subQ0=sQuery(id+"F15.wireOp",EDGE,"E25");var subQ1=makeQuery(id+"F14.opExtrude","CAP_EDGE",EDGE,{"disambiguationData":[OSD([sQuery(id+"F13.wireOp",EDGE,"E19")])],"isStart":false});var subQ2=makeQuery(id+"F15.imprint","INTERSECT",VERTEX,{"derivedFrom":[subQ1,subQ0]});Q5=makeQuery(id+"F15.imprint","IMPRINT",FACE,{"disambiguationData":[TD([[makeQuery(id+"F15.imprint","IMPRINT",EDGE,{"disambiguationData":[TD([[subQ2,-1.0]])],"derivedFrom":subQ1}),1.0]])]});}
            var Q6;
            {var subQ0=sQuery(id+"F15.wireOp",EDGE,"E24");var subQ1=makeQuery(id+"F14.opExtrude","CAP_EDGE",EDGE,{"disambiguationData":[OSD([sQuery(id+"F13.wireOp",EDGE,"E19")])],"isStart":false});var subQ2=makeQuery(id+"F15.imprint","INTERSECT",VERTEX,{"derivedFrom":[subQ1,subQ0]});Q6=makeQuery(id+"F15.imprint","IMPRINT",FACE,{"disambiguationData":[TD([[makeQuery(id+"F15.imprint","IMPRINT",EDGE,{"disambiguationData":[TD([[subQ2,-1.0]])],"derivedFrom":subQ1}),1.0]])]});}
            var Q7;
            {var subQ0=sQuery(id+"F15.wireOp",EDGE,"E23");var subQ1=makeQuery(id+"F14.opExtrude","CAP_EDGE",EDGE,{"disambiguationData":[OSD([sQuery(id+"F13.wireOp",EDGE,"E19")])],"isStart":false});var subQ2=makeQuery(id+"F15.imprint","INTERSECT",VERTEX,{"derivedFrom":[subQ1,subQ0]});Q7=makeQuery(id+"F15.imprint","IMPRINT",FACE,{"disambiguationData":[TD([[makeQuery(id+"F15.imprint","IMPRINT",EDGE,{"disambiguationData":[TD([[subQ2,-1.0]])],"derivedFrom":subQ1}),1.0]])]});}
            var Q8;
            {var subQ0=sQuery(id+"F15.wireOp",EDGE,"E29");var subQ1=sQuery(id+"F15.wireOp",EDGE,"E23");var subQ2=makeQuery(id+"F15.imprint","INTERSECT",VERTEX,{"derivedFrom":[subQ1,subQ0,sQuery(id+"F15.wireOp",EDGE,"E32")]});Q8=makeQuery(id+"F15.imprint","IMPRINT",FACE,{"disambiguationData":[TD([[makeQuery(id+"F15.imprint","IMPRINT",EDGE,{"disambiguationData":[TD([[subQ2,-1.0]])],"derivedFrom":subQ1}),1.0]])]});}
            var Q9;
            {var subQ0=sQuery(id+"F15.wireOp",EDGE,"E28");var subQ1=sQuery(id+"F15.wireOp",EDGE,"E24");var subQ2=makeQuery(id+"F15.imprint","INTERSECT",VERTEX,{"derivedFrom":[subQ1,subQ0,sQuery(id+"F15.wireOp",EDGE,"E32")]});Q9=makeQuery(id+"F15.imprint","IMPRINT",FACE,{"disambiguationData":[TD([[makeQuery(id+"F15.imprint","IMPRINT",EDGE,{"disambiguationData":[TD([[subQ2,-1.0]])],"derivedFrom":subQ1}),1.0]])]});}
            var Q10;
            {var subQ0=sQuery(id+"F15.wireOp",EDGE,"E30");var subQ1=sQuery(id+"F15.wireOp",EDGE,"E22");var subQ2=makeQuery(id+"F15.imprint","INTERSECT",VERTEX,{"derivedFrom":[subQ1,subQ0,sQuery(id+"F15.wireOp",EDGE,"E32")]});Q10=makeQuery(id+"F15.imprint","IMPRINT",FACE,{"disambiguationData":[TD([[makeQuery(id+"F15.imprint","IMPRINT",EDGE,{"disambiguationData":[TD([[subQ2,-1.0]])],"derivedFrom":subQ1}),1.0]])]});}
            var Q11;
            {var subQ0=sQuery(id+"F15.wireOp",EDGE,"E29");var subQ1=sQuery(id+"F15.wireOp",EDGE,"E22");var subQ2=makeQuery(id+"F15.imprint","INTERSECT",VERTEX,{"derivedFrom":[subQ1,subQ0,sQuery(id+"F15.wireOp",EDGE,"E33")]});Q11=makeQuery(id+"F15.imprint","IMPRINT",FACE,{"disambiguationData":[TD([[makeQuery(id+"F15.imprint","IMPRINT",EDGE,{"disambiguationData":[TD([[subQ2,-1.0]])],"derivedFrom":subQ1}),1.0]])]});}
            var Q12;
            {var subQ0=sQuery(id+"F15.wireOp",EDGE,"E28");var subQ1=sQuery(id+"F15.wireOp",EDGE,"E23");var subQ2=makeQuery(id+"F15.imprint","INTERSECT",VERTEX,{"derivedFrom":[subQ1,subQ0,sQuery(id+"F15.wireOp",EDGE,"E33")]});Q12=makeQuery(id+"F15.imprint","IMPRINT",FACE,{"disambiguationData":[TD([[makeQuery(id+"F15.imprint","IMPRINT",EDGE,{"disambiguationData":[TD([[subQ2,-1.0]])],"derivedFrom":subQ1}),1.0]])]});}
            var Q13;
            {var subQ0=sQuery(id+"F15.wireOp",EDGE,"E28");var subQ1=sQuery(id+"F15.wireOp",EDGE,"E22");var subQ2=makeQuery(id+"F15.imprint","INTERSECT",VERTEX,{"derivedFrom":[subQ1,subQ0,sQuery(id+"F15.wireOp",EDGE,"E34")]});Q13=makeQuery(id+"F15.imprint","IMPRINT",FACE,{"disambiguationData":[TD([[makeQuery(id+"F15.imprint","IMPRINT",EDGE,{"disambiguationData":[TD([[subQ2,-1.0]])],"derivedFrom":subQ1}),1.0]])]});}
            var Q14;
            {var subQ5=sQuery(id+"F15.wireOp",EDGE,"E36");Q14=makeQuery(id+"F15.imprint","IMPRINT",FACE,{"disambiguationData":[TD([[makeQuery(id+"F15.imprint","IMPRINT",EDGE,{"derivedFrom":subQ5}),-1.0]])]});}
            extrude(context, id + "F18", {"entities" : qUnion([Q0, Q1, Q2, Q3, Q4, Q5, Q6, Q7, Q8, Q9, Q10, Q11, Q12, Q13, Q14]), "depth" : 0.4 * mm, "offsetDistance" : 25.4 * mm});
        }
    });
